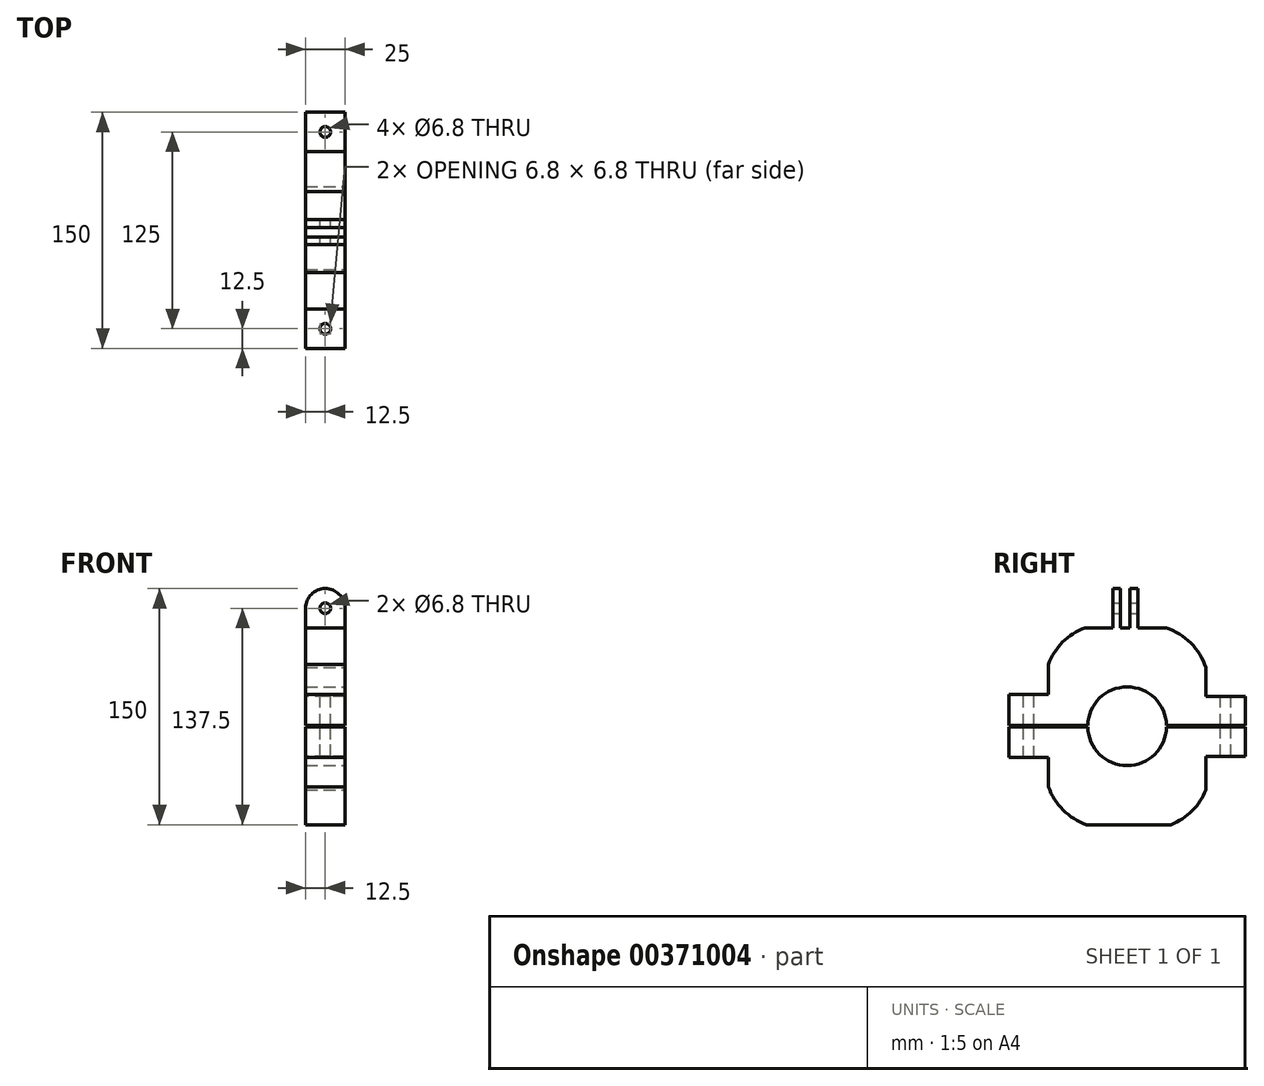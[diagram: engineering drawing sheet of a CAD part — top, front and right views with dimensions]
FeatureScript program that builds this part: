
annotation { "Feature Type Name" : "Feature", "Feature Type Description" : "" }
export const myFeature = defineFeature(function(context is Context, id is Id, definition is map)
    precondition{}
    {
        {
            var Q0;
            Q0=qCreatedBy(makeId("Right.planeOp"),FACE);
            var sketch = newSketch(context, id + "F0", { "sketchPlane" : qUnion([Q0])});
            skLineSegment(sketch, "E0.bottom", {"start": v(50, 62.5) * mm, "end": v(-50, 62.5) * mm});
            skLineSegment(sketch, "E0.top", {"start": v(50, -62.5) * mm, "end": v(-50, -62.5) * mm});
            skLineSegment(sketch, "E0.left", {"start": v(50, 62.5) * mm, "end": v(50, -62.5) * mm});
            skLineSegment(sketch, "E0.right", {"start": v(-50, 62.5) * mm, "end": v(-50, -62.5) * mm});
            skPoint(sketch, "E0.middle", {"position": v(0, 0) * mm});
            skSolve(sketch);
        }
        {
            var Q0;
            Q0 = qSketchRegion(id + "F0", true);
            extrude(context, id + "F1", {"entities" : qUnion([Q0]), "depth" : 25 * mm});
        }
        {
            var Q0;
            Q0=makeQuery(id+"F1.opExtrude","CAP_FACE",FACE,{"disambiguationData":[OSD([sQuery(id+"F0.wireOp",EDGE,"E0.bottom"),sQuery(id+"F0.wireOp",EDGE,"E0.top"),sQuery(id+"F0.wireOp",EDGE,"E0.left"),sQuery(id+"F0.wireOp",EDGE,"E0.right")])],"isStart":false});
            var sketch = newSketch(context, id + "F2", { "sketchPlane" : qUnion([Q0])});
            skCircle(sketch, "E1", {"center": v(0, 0) * mm, "radius": 25 * mm});
            skSolve(sketch);
        }
        {
            var Q0;
            Q0=makeQuery(id+"F2.imprint","IMPRINT",FACE,{"disambiguationData":[TD([[makeQuery(id+"F2.imprint","IMPRINT",EDGE,{"derivedFrom":sQuery(id+"F2.wireOp",EDGE,"E1")}),1.0]])]});
            extrude(context, id + "F3", {"entities" : qUnion([Q0]), "operationType" : NewBodyOperationType.REMOVE, "endBound" : BoundingType.THROUGH_ALL, "oppositeDirection" : true, "depth" : 25 * mm});
        }
        {
            var Q0;
            Q0=makeQuery(id+"F1.opExtrude","CAP_FACE",FACE,{"disambiguationData":[OSD([sQuery(id+"F0.wireOp",EDGE,"E0.bottom"),sQuery(id+"F0.wireOp",EDGE,"E0.top"),sQuery(id+"F0.wireOp",EDGE,"E0.left"),sQuery(id+"F0.wireOp",EDGE,"E0.right")])],"isStart":false});
            var sketch = newSketch(context, id + "F4", { "sketchPlane" : qUnion([Q0])});
            skPoint(sketch, "E2", {"position": v(-50, 12.5) * mm});
            skPoint(sketch, "E3", {"position": v(0, 62.5) * mm});
            skArc(sketch, "E4", {"start": v(0, 62.5) * mm, "mid": v(-40.95, 53.45) * mm, "end": v(-50, 12.5) * mm});
            skPoint(sketch, "E5", {"position": v(50, 12.5) * mm});
            skArc(sketch, "E6", {"start": v(50, 12.5) * mm, "mid": v(40.4, 52.9) * mm, "end": v(0, 62.5) * mm});
            skPoint(sketch, "E7", {"position": v(-50, -12.5) * mm});
            skPoint(sketch, "E8", {"position": v(0, -62.5) * mm});
            skPoint(sketch, "E9", {"position": v(50, -12.5) * mm});
            skArc(sketch, "E10", {"start": v(-50, -12.5) * mm, "mid": v(-40.7, -53.2) * mm, "end": v(0, -62.5) * mm});
            skArc(sketch, "E11", {"start": v(0, -62.5) * mm, "mid": v(41.25, -53.75) * mm, "end": v(50, -12.5) * mm});
            skSolve(sketch);
        }
        {
            var Q0;
            Q0 = qSketchRegion(id + "F4", true);
            var Q1;
            {var subQ0=sQuery(id+"F4.wireOp",EDGE,"E4");var subQ1=makeQuery(id+"F1.opExtrude","CAP_EDGE",EDGE,{"disambiguationData":[OSD([sQuery(id+"F0.wireOp",EDGE,"E0.bottom")])],"isStart":false});var subQ2=makeQuery(id+"F4.imprint","INTERSECT",VERTEX,{"disambiguationData":[OD(1.0)],"derivedFrom":[subQ1,subQ0]});Q1=makeQuery(id+"F4.imprint","IMPRINT",FACE,{"disambiguationData":[TD([[makeQuery(id+"F4.imprint","IMPRINT",EDGE,{"disambiguationData":[TD([[subQ2,-1.0]])],"derivedFrom":subQ0}),-1.0]])]});}
            var Q2;
            {var subQ0=sQuery(id+"F4.wireOp",EDGE,"E6");var subQ1=makeQuery(id+"F1.opExtrude","CAP_EDGE",EDGE,{"disambiguationData":[OSD([sQuery(id+"F0.wireOp",EDGE,"E0.left")])],"isStart":false});var subQ2=makeQuery(id+"F4.imprint","INTERSECT",VERTEX,{"disambiguationData":[OD(1.0)],"derivedFrom":[subQ1,subQ0]});Q2=makeQuery(id+"F4.imprint","IMPRINT",FACE,{"disambiguationData":[TD([[makeQuery(id+"F4.imprint","IMPRINT",EDGE,{"disambiguationData":[TD([[subQ2,-1.0]])],"derivedFrom":subQ0}),-1.0]])]});}
            var Q3;
            {var subQ0=sQuery(id+"F4.wireOp",EDGE,"E11");var subQ1=makeQuery(id+"F1.opExtrude","CAP_EDGE",EDGE,{"disambiguationData":[OSD([sQuery(id+"F0.wireOp",EDGE,"E0.top")])],"isStart":false});var subQ2=makeQuery(id+"F4.imprint","INTERSECT",VERTEX,{"disambiguationData":[OD(1.0)],"derivedFrom":[subQ1,subQ0]});Q3=makeQuery(id+"F4.imprint","IMPRINT",FACE,{"disambiguationData":[TD([[makeQuery(id+"F4.imprint","IMPRINT",EDGE,{"disambiguationData":[TD([[subQ2,-1.0]])],"derivedFrom":subQ0}),-1.0]])]});}
            var Q4;
            {var subQ0=sQuery(id+"F4.wireOp",EDGE,"E10");var subQ1=makeQuery(id+"F1.opExtrude","CAP_EDGE",EDGE,{"disambiguationData":[OSD([sQuery(id+"F0.wireOp",EDGE,"E0.right")])],"isStart":false});var subQ2=makeQuery(id+"F4.imprint","INTERSECT",VERTEX,{"disambiguationData":[OD(1.0)],"derivedFrom":[subQ1,subQ0]});Q4=makeQuery(id+"F4.imprint","IMPRINT",FACE,{"disambiguationData":[TD([[makeQuery(id+"F4.imprint","IMPRINT",EDGE,{"disambiguationData":[TD([[subQ2,-1.0]])],"derivedFrom":subQ0}),-1.0]])]});}
            extrude(context, id + "F5", {"entities" : qUnion([Q0, Q1, Q2, Q3, Q4]), "operationType" : NewBodyOperationType.REMOVE, "endBound" : BoundingType.THROUGH_ALL, "oppositeDirection" : true, "depth" : 25 * mm});
        }
        {
            var Q0;
            Q0=makeQuery(id+"F1.opExtrude","SWEPT_FACE",FACE,{"disambiguationData":[OSD([sQuery(id+"F0.wireOp",EDGE,"E0.right")])]});
            var sketch = newSketch(context, id + "F6", { "sketchPlane" : qUnion([Q0])});
            skLineSegment(sketch, "E12.bottom", {"start": v(0, 20.14) * mm, "end": v(25, 20.14) * mm});
            skLineSegment(sketch, "E12.top", {"start": v(0, -19.86) * mm, "end": v(25, -19.86) * mm});
            skLineSegment(sketch, "E12.left", {"start": v(0, 20.14) * mm, "end": v(0, -19.86) * mm});
            skLineSegment(sketch, "E12.right", {"start": v(25, 20.14) * mm, "end": v(25, -19.86) * mm});
            skSolve(sketch);
        }
        {
            var Q0;
            Q0=makeQuery(id+"F6.imprint","IMPRINT",FACE,{"disambiguationData":[TD([[makeQuery(id+"F6.imprint","IMPRINT",EDGE,{"derivedFrom":sQuery(id+"F6.wireOp",EDGE,"E12.bottom")}),-1.0]])]});
            extrude(context, id + "F7", {"entities" : qUnion([Q0]), "operationType" : NewBodyOperationType.ADD, "depth" : 25 * mm});
        }
        {
            var Q0;
            Q0=makeQuery(id+"F1.opExtrude","SWEPT_FACE",FACE,{"disambiguationData":[OSD([sQuery(id+"F0.wireOp",EDGE,"E0.left")])]});
            var sketch = newSketch(context, id + "F8", { "sketchPlane" : qUnion([Q0])});
            skLineSegment(sketch, "E13.bottom", {"start": v(-25, 18.92) * mm, "end": v(0, 18.92) * mm});
            skLineSegment(sketch, "E13.top", {"start": v(-25, -19.08) * mm, "end": v(0, -19.08) * mm});
            skLineSegment(sketch, "E13.left", {"start": v(-25, 18.92) * mm, "end": v(-25, -19.08) * mm});
            skLineSegment(sketch, "E13.right", {"start": v(0, 18.92) * mm, "end": v(0, -19.08) * mm});
            skSolve(sketch);
        }
        {
            var Q0;
            Q0 = qSketchRegion(id + "F8", true);
            extrude(context, id + "F9", {"entities" : qUnion([Q0]), "operationType" : NewBodyOperationType.ADD, "depth" : 25 * mm});
        }
        {
            var Q0;
            Q0=makeQuery(id+"F9.opExtrude","CAP_FACE",FACE,{"disambiguationData":[OSD([sQuery(id+"F8.wireOp",EDGE,"E13.bottom"),sQuery(id+"F8.wireOp",EDGE,"E13.top"),sQuery(id+"F8.wireOp",EDGE,"E13.left"),sQuery(id+"F8.wireOp",EDGE,"E13.right")])],"isStart":false});
            var sketch = newSketch(context, id + "F10", { "sketchPlane" : qUnion([Q0])});
            skLineSegment(sketch, "E14.bottom", {"start": v(-25, 0.5) * mm, "end": v(0, 0.5) * mm});
            skLineSegment(sketch, "E14.top", {"start": v(-25, -0.5) * mm, "end": v(0, -0.5) * mm});
            skLineSegment(sketch, "E14.left", {"start": v(-25, 0.5) * mm, "end": v(-25, -0.5) * mm});
            skLineSegment(sketch, "E14.right", {"start": v(0, 0.5) * mm, "end": v(0, -0.5) * mm});
            skSolve(sketch);
        }
        {
            var Q0;
            Q0 = qSketchRegion(id + "F10", true);
            extrude(context, id + "F11", {"entities" : qUnion([Q0]), "operationType" : NewBodyOperationType.REMOVE, "endBound" : BoundingType.THROUGH_ALL, "oppositeDirection" : true, "depth" : 25 * mm});
        }
        {
            var Q0;
            Q0=makeQuery(id+"F9.opExtrude","SWEPT_FACE",FACE,{"disambiguationData":[OSD([sQuery(id+"F8.wireOp",EDGE,"E13.bottom")])]});
            var sketch = newSketch(context, id + "F12", { "sketchPlane" : qUnion([Q0])});
            skPoint(sketch, "E15", {"position": v(25, 62.5) * mm});
            skPoint(sketch, "E16", {"position": v(12.5, 75) * mm});
            skPoint(sketch, "E17", {"position": v(12.5, 62.5) * mm});
            skCircle(sketch, "E18", {"center": v(12.5, 62.5) * mm, "radius": 3.4 * mm});
            skSolve(sketch);
        }
        {
            var Q0;
            Q0 = qSketchRegion(id + "F12", true);
            extrude(context, id + "F13", {"entities" : qUnion([Q0]), "operationType" : NewBodyOperationType.REMOVE, "oppositeDirection" : true, "depth" : 60 * mm});
        }
        {
            var Q0;
            Q0=makeQuery(id+"F7.opExtrude","SWEPT_FACE",FACE,{"disambiguationData":[OSD([sQuery(id+"F6.wireOp",EDGE,"E12.bottom")])]});
            var sketch = newSketch(context, id + "F14", { "sketchPlane" : qUnion([Q0])});
            skPoint(sketch, "E19", {"position": v(25, -62.5) * mm});
            skPoint(sketch, "E20", {"position": v(12.5, -75) * mm});
            skPoint(sketch, "E21", {"position": v(12.5, -62.5) * mm});
            skCircle(sketch, "E22", {"center": v(12.5, -62.5) * mm, "radius": 3.4 * mm});
            skSolve(sketch);
        }
        {
            var Q0;
            Q0 = qSketchRegion(id + "F14", true);
            extrude(context, id + "F15", {"entities" : qUnion([Q0]), "operationType" : NewBodyOperationType.REMOVE, "endBound" : BoundingType.THROUGH_ALL, "oppositeDirection" : true, "depth" : 25 * mm});
        }
        {
            var Q0;
            Q0=makeQuery(id+"F7.opExtrude","SWEPT_FACE",FACE,{"disambiguationData":[OSD([sQuery(id+"F6.wireOp",EDGE,"E12.top")])]});
            var sketch = newSketch(context, id + "F16", { "sketchPlane" : qUnion([Q0])});
            skPoint(sketch, "E23", {"position": v(25, 62.5) * mm});
            skPoint(sketch, "E24", {"position": v(12.5, 75) * mm});
            skPoint(sketch, "E25", {"position": v(12.5, 62.5) * mm});
            skCircle(sketch, "E26", {"center": v(12.5, 62.5) * mm, "radius": 3.4 * mm});
            skSolve(sketch);
        }
        {
            var Q0;
            Q0 = qSketchRegion(id + "F16", true);
            extrude(context, id + "F17", {"entities" : qUnion([Q0]), "operationType" : NewBodyOperationType.REMOVE, "endBound" : BoundingType.THROUGH_ALL, "oppositeDirection" : true, "depth" : 25 * mm});
        }
        {
            var Q0;
            Q0=makeQuery(id+"F9.opExtrude","SWEPT_FACE",FACE,{"disambiguationData":[OSD([sQuery(id+"F8.wireOp",EDGE,"E13.top")])]});
            var sketch = newSketch(context, id + "F18", { "sketchPlane" : qUnion([Q0])});
            skPoint(sketch, "E27", {"position": v(25, -62.5) * mm});
            skPoint(sketch, "E28", {"position": v(12.5, -75) * mm});
            skPoint(sketch, "E29", {"position": v(12.5, -62.5) * mm});
            skCircle(sketch, "E30", {"center": v(12.5, -62.5) * mm, "radius": 3.4 * mm});
            skSolve(sketch);
        }
        {
            var Q0;
            Q0 = qSketchRegion(id + "F18", true);
            extrude(context, id + "F19", {"entities" : qUnion([Q0]), "operationType" : NewBodyOperationType.REMOVE, "endBound" : BoundingType.THROUGH_ALL, "oppositeDirection" : true, "depth" : 25 * mm});
        }
        {
            var Q0;
            Q0=makeQuery(id+"F1.opExtrude","SWEPT_FACE",FACE,{"disambiguationData":[OSD([sQuery(id+"F0.wireOp",EDGE,"E0.bottom")])]});
            var sketch = newSketch(context, id + "F20", { "sketchPlane" : qUnion([Q0])});
            skLineSegment(sketch, "E31.bottom", {"start": v(0, -16.16) * mm, "end": v(25, -16.16) * mm});
            skLineSegment(sketch, "E31.top", {"start": v(0, 13.84) * mm, "end": v(25, 13.84) * mm});
            skLineSegment(sketch, "E31.left", {"start": v(0, -16.16) * mm, "end": v(0, 13.84) * mm});
            skLineSegment(sketch, "E31.right", {"start": v(25, -16.16) * mm, "end": v(25, 13.84) * mm});
            skSolve(sketch);
        }
        {
            var Q0;
            Q0 = qSketchRegion(id + "F20", true);
            extrude(context, id + "F21", {"entities" : qUnion([Q0]), "operationType" : NewBodyOperationType.ADD, "depth" : 25 * mm});
        }
        {
            var Q0;
            Q0=makeQuery(id+"F21.opExtrude","CAP_FACE",FACE,{"disambiguationData":[OSD([sQuery(id+"F20.wireOp",EDGE,"E31.bottom"),sQuery(id+"F20.wireOp",EDGE,"E31.top"),sQuery(id+"F20.wireOp",EDGE,"E31.left"),sQuery(id+"F20.wireOp",EDGE,"E31.right")])],"isStart":false});
            var sketch = newSketch(context, id + "F22", { "sketchPlane" : qUnion([Q0])});
            skLineSegment(sketch, "E32.bottom", {"start": v(0, -9.16) * mm, "end": v(25, -9.16) * mm});
            skLineSegment(sketch, "E32.top", {"start": v(0, -4.16) * mm, "end": v(25, -4.16) * mm});
            skLineSegment(sketch, "E32.left", {"start": v(0, -9.16) * mm, "end": v(0, -4.16) * mm});
            skLineSegment(sketch, "E32.right", {"start": v(25, -9.16) * mm, "end": v(25, -4.16) * mm});
            skLineSegment(sketch, "E33.bottom", {"start": v(0, 1.84) * mm, "end": v(25, 1.84) * mm});
            skLineSegment(sketch, "E33.top", {"start": v(0, 6.84) * mm, "end": v(25, 6.84) * mm});
            skLineSegment(sketch, "E33.left", {"start": v(0, 1.84) * mm, "end": v(0, 6.84) * mm});
            skLineSegment(sketch, "E33.right", {"start": v(25, 1.84) * mm, "end": v(25, 6.84) * mm});
            skSolve(sketch);
        }
        {
            var Q0;
            Q0=makeQuery(id+"F21.opExtrude","SWEPT_FACE",FACE,{"disambiguationData":[OSD([sQuery(id+"F20.wireOp",EDGE,"E31.top")])]});
            var sketch = newSketch(context, id + "F23", { "sketchPlane" : qUnion([Q0])});
            skPoint(sketch, "E34", {"position": v(-12.5, 87.5) * mm});
            skPoint(sketch, "E35", {"position": v(0, 75) * mm});
            skPoint(sketch, "E36", {"position": v(-25, 75) * mm});
            skCircle(sketch, "E37", {"center": v(-12.5, 75) * mm, "radius": 12.5 * mm});
            skSolve(sketch);
        }
        {
            var Q0;
            {var subQ0=sQuery(id+"F23.wireOp",EDGE,"E37");var subQ1=sQuery(id+"F20.wireOp",EDGE,"E31.top");var subQ2=makeQuery(id+"F21.opExtrude","CAP_EDGE",EDGE,{"disambiguationData":[OSD([subQ1])],"isStart":false});var subQ3=makeQuery(id+"F23.imprint","INTERSECT",VERTEX,{"derivedFrom":[subQ2,subQ0]});Q0=makeQuery(id+"F23.imprint","IMPRINT",FACE,{"disambiguationData":[TD([[makeQuery(id+"F23.imprint","IMPRINT",EDGE,{"disambiguationData":[TD([[subQ3,1.0]])],"derivedFrom":subQ0}),-1.0]])]});}
            var Q1;
            {var subQ0=sQuery(id+"F23.wireOp",EDGE,"E37");var subQ1=sQuery(id+"F20.wireOp",EDGE,"E31.top");var subQ2=makeQuery(id+"F21.opExtrude","CAP_EDGE",EDGE,{"disambiguationData":[OSD([subQ1])],"isStart":false});var subQ3=makeQuery(id+"F23.imprint","INTERSECT",VERTEX,{"derivedFrom":[subQ2,subQ0]});Q1=makeQuery(id+"F23.imprint","IMPRINT",FACE,{"disambiguationData":[TD([[makeQuery(id+"F23.imprint","IMPRINT",EDGE,{"disambiguationData":[TD([[subQ3,-1.0]])],"derivedFrom":subQ0}),-1.0]])]});}
            extrude(context, id + "F24", {"entities" : qUnion([Q0, Q1]), "operationType" : NewBodyOperationType.REMOVE, "endBound" : BoundingType.THROUGH_ALL, "oppositeDirection" : true, "depth" : 25 * mm});
        }
        {
            var Q0;
            {var subQ0=sQuery(id+"F22.wireOp",EDGE,"E32.bottom");Q0=makeQuery(id+"F22.imprint","IMPRINT",FACE,{"disambiguationData":[TD([[makeQuery(id+"F22.imprint","IMPRINT",EDGE,{"derivedFrom":subQ0}),-1.0]])]});}
            var Q1;
            {var subQ0=sQuery(id+"F22.wireOp",EDGE,"E32.top");Q1=makeQuery(id+"F22.imprint","IMPRINT",FACE,{"disambiguationData":[TD([[makeQuery(id+"F22.imprint","IMPRINT",EDGE,{"derivedFrom":subQ0}),1.0]])]});}
            var Q2;
            {var subQ0=sQuery(id+"F22.wireOp",EDGE,"E33.top");Q2=makeQuery(id+"F22.imprint","IMPRINT",FACE,{"disambiguationData":[TD([[makeQuery(id+"F22.imprint","IMPRINT",EDGE,{"derivedFrom":subQ0}),1.0]])]});}
            extrude(context, id + "F25", {"entities" : qUnion([Q0, Q1, Q2]), "operationType" : NewBodyOperationType.REMOVE, "oppositeDirection" : true, "depth" : 25 * mm});
        }
        {
            var Q0;
            Q0=makeQuery(id+"F25.boolean.opBoolean","COPY",FACE,{"derivedFrom":makeQuery(id+"F25.opExtrude","SWEPT_FACE",FACE,{"disambiguationData":[OSD([sQuery(id+"F22.wireOp",EDGE,"E33.top")])]})});
            var sketch = newSketch(context, id + "F26", { "sketchPlane" : qUnion([Q0])});
            skPoint(sketch, "E38", {"position": v(0, 75) * mm});
            skPoint(sketch, "E39", {"position": v(-25, 75) * mm});
            skPoint(sketch, "E40", {"position": v(-12.5, 75) * mm});
            skCircle(sketch, "E41", {"center": v(-12.5, 75) * mm, "radius": 3.4 * mm});
            skSolve(sketch);
        }
        {
            var Q0;
            Q0 = qSketchRegion(id + "F26", true);
            extrude(context, id + "F27", {"entities" : qUnion([Q0]), "operationType" : NewBodyOperationType.REMOVE, "endBound" : BoundingType.THROUGH_ALL, "oppositeDirection" : true, "depth" : 25 * mm});
        }
    });
